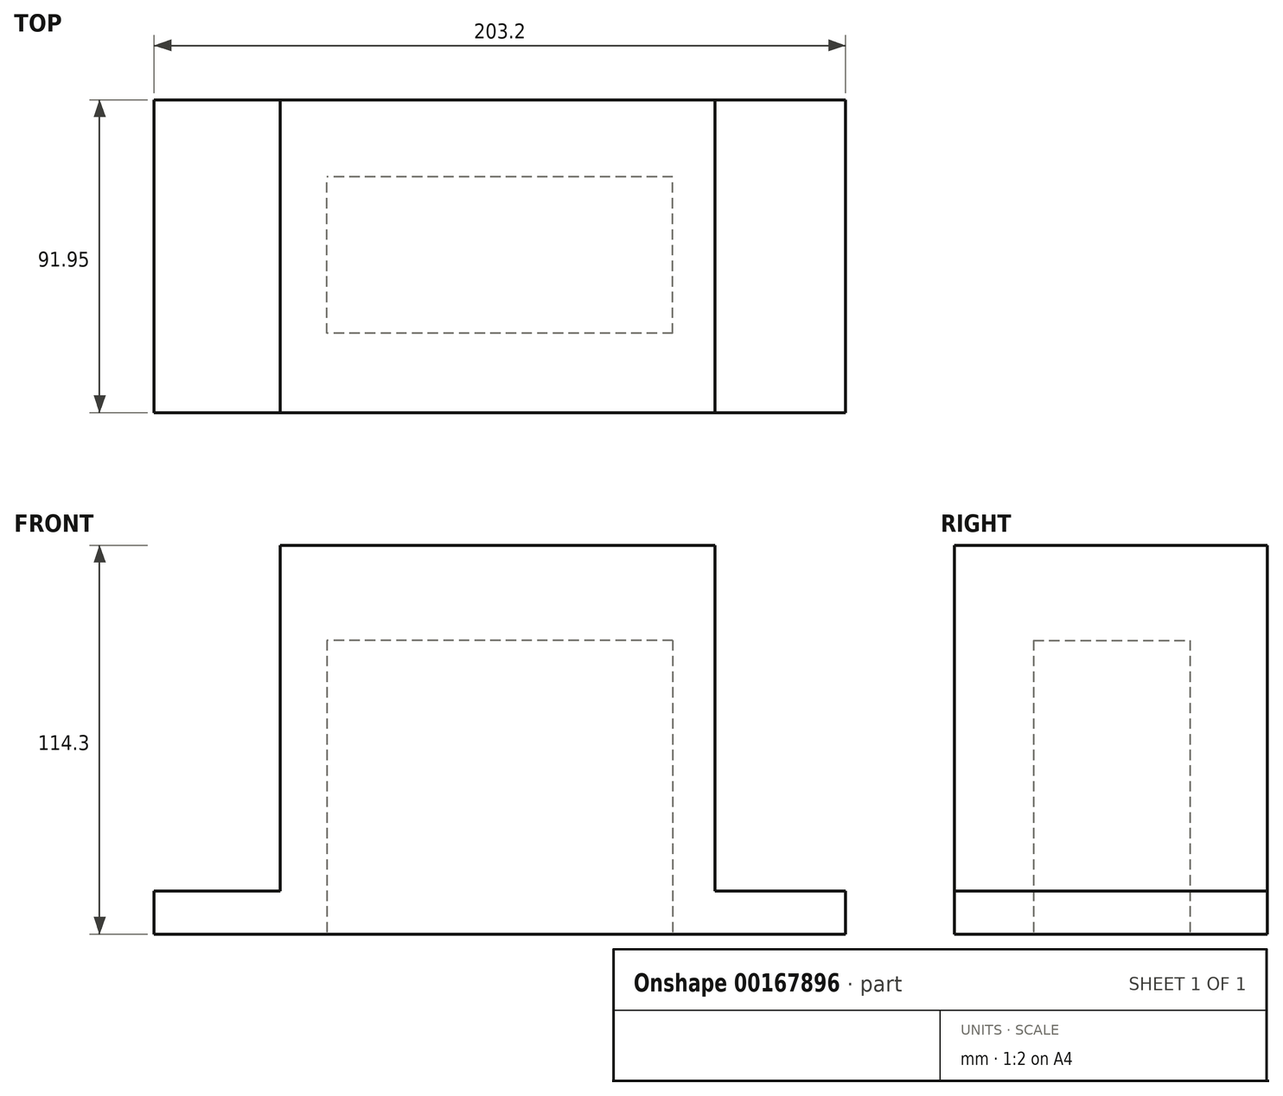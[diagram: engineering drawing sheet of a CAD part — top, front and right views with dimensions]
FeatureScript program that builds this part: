
annotation { "Feature Type Name" : "Feature", "Feature Type Description" : "" }
export const myFeature = defineFeature(function(context is Context, id is Id, definition is map)
    precondition{}
    {
        {
            var Q0;
            Q0=qCreatedBy(makeId("Front.planeOp"),FACE);
            var sketch = newSketch(context, id + "F0", { "sketchPlane" : qUnion([Q0])});
            skLineSegment(sketch, "E0.bottom", {"start": v(76.2, 57.15) * mm, "end": v(-76.2, 57.15) * mm});
            skLineSegment(sketch, "E0.top", {"start": v(76.2, -57.15) * mm, "end": v(-76.2, -57.15) * mm});
            skLineSegment(sketch, "E0.left", {"start": v(76.2, 57.15) * mm, "end": v(76.2, -57.15) * mm});
            skLineSegment(sketch, "E0.right", {"start": v(-76.2, 57.15) * mm, "end": v(-76.2, -57.15) * mm});
            skPoint(sketch, "E0.middle", {"position": v(0, 0) * mm});
            skSolve(sketch);
        }
        {
            var Q0;
            Q0=makeQuery(id+"F0.imprint","IMPRINT",FACE,{"disambiguationData":[TD([[makeQuery(id+"F0.imprint","IMPRINT",EDGE,{"derivedFrom":sQuery(id+"F0.wireOp",EDGE,"E0.bottom")}),1.0]])]});
            extrude(context, id + "F1", {"entities" : qUnion([Q0]), "oppositeDirection" : true, "depth" : 91.95 * mm});
        }
        {
            var Q0;
            Q0=makeQuery(id+"F1.opExtrude","SWEPT_FACE",FACE,{"disambiguationData":[OSD([sQuery(id+"F0.wireOp",EDGE,"E0.left")])]});
            var sketch = newSketch(context, id + "F2", { "sketchPlane" : qUnion([Q0])});
            skLineSegment(sketch, "E1", {"start": v(0, -57.15) * mm, "end": v(0, -44.45) * mm});
            skLineSegment(sketch, "E2", {"start": v(0, -44.45) * mm, "end": v(-62.9, -1.45) * mm});
            skLineSegment(sketch, "E3", {"start": v(-62.9, -1.45) * mm, "end": v(-62.9, 98.04) * mm});
            skLineSegment(sketch, "E4", {"start": v(-62.9, 98.04) * mm, "end": v(31.97, 98.04) * mm});
            skLineSegment(sketch, "E5", {"start": v(31.97, 98.04) * mm, "end": v(91.95, 57.15) * mm});
            skLineSegment(sketch, "E6", {"start": v(91.95, 57.15) * mm, "end": v(91.95, -44.45) * mm});
            skLineSegment(sketch, "E7", {"start": v(91.95, -44.45) * mm, "end": v(0, -44.45) * mm});
            skSolve(sketch);
        }
        {
            var Q0;
            Q0=makeQuery(id+"F2.imprint","IMPRINT",FACE,{"disambiguationData":[TD([[makeQuery(id+"F2.imprint","IMPRINT",EDGE,{"derivedFrom":sQuery(id+"F2.wireOp",EDGE,"E6")}),-1.0]])]});
            extrude(context, id + "F3", {"entities" : qUnion([Q0]), "operationType" : NewBodyOperationType.REMOVE, "oppositeDirection" : true, "depth" : 37.08 * mm});
        }
        {
            var Q0;
            Q0=makeQuery(id+"F1.opExtrude","SWEPT_FACE",FACE,{"disambiguationData":[OSD([sQuery(id+"F0.wireOp",EDGE,"E0.right")])]});
            var sketch = newSketch(context, id + "F4", { "sketchPlane" : qUnion([Q0])});
            skLineSegment(sketch, "E8", {"start": v(0, -57.15) * mm, "end": v(0, -44.45) * mm});
            skLineSegment(sketch, "E9", {"start": v(0, -44.45) * mm, "end": v(87.77, 57.15) * mm});
            skLineSegment(sketch, "E10", {"start": v(0, -44.45) * mm, "end": v(-91.95, -44.45) * mm});
            skSolve(sketch);
        }
        {
            var Q0;
            {var subQ0=sQuery(id+"F4.wireOp",EDGE,"E10");Q0=makeQuery(id+"F4.imprint","IMPRINT",FACE,{"disambiguationData":[TD([[makeQuery(id+"F4.imprint","IMPRINT",EDGE,{"derivedFrom":subQ0}),-1.0]])]});}
            extrude(context, id + "F5", {"entities" : qUnion([Q0]), "operationType" : NewBodyOperationType.REMOVE, "oppositeDirection" : true, "depth" : 37.08 * mm});
        }
        {
            var Q0;
            Q0=makeQuery(id+"F3.boolean.opBoolean","COPY",FACE,{"derivedFrom":makeQuery(id+"F3.opExtrude","CAP_FACE",FACE,{"disambiguationData":[OSD([sQuery(id+"F0.wireOp",EDGE,"E0.bottom"),sQuery(id+"F0.wireOp",EDGE,"E0.left"),sQuery(id+"F2.wireOp",EDGE,"E6"),sQuery(id+"F2.wireOp",EDGE,"E7")])],"isStart":false})});
            extrude(context, id + "F6", {"entities" : qUnion([Q0]), "operationType" : NewBodyOperationType.ADD, "depth" : 24.13 * mm});
        }
        {
            var Q0;
            Q0=makeQuery(id+"F5.boolean.opBoolean","COPY",FACE,{"derivedFrom":makeQuery(id+"F5.opExtrude","CAP_FACE",FACE,{"disambiguationData":[OSD([sQuery(id+"F0.wireOp",EDGE,"E0.bottom"),sQuery(id+"F0.wireOp",EDGE,"E0.right"),sQuery(id+"F4.wireOp",EDGE,"E10")])],"isStart":false})});
            extrude(context, id + "F7", {"entities" : qUnion([Q0]), "operationType" : NewBodyOperationType.ADD, "depth" : 25.4 * mm});
        }
        {
            var Q0;
            Q0=makeQuery(id+"F1.opExtrude","SWEPT_FACE",FACE,{"disambiguationData":[OSD([sQuery(id+"F0.wireOp",EDGE,"E0.left")])]});
            extrude(context, id + "F8", {"entities" : qUnion([Q0]), "operationType" : NewBodyOperationType.ADD, "depth" : 25.4 * mm});
        }
        {
            var Q0;
            Q0=makeQuery(id+"F1.opExtrude","SWEPT_FACE",FACE,{"disambiguationData":[OSD([sQuery(id+"F0.wireOp",EDGE,"E0.right")])]});
            extrude(context, id + "F9", {"entities" : qUnion([Q0]), "operationType" : NewBodyOperationType.ADD, "depth" : 25.4 * mm});
        }
        {
            var Q0;
            {var subQ0=sQuery(id+"F0.wireOp",EDGE,"E0.top");Q0=makeQuery(id+"F9.boolean.opBoolean","MERGE",FACE,{"derivedFrom":[makeQuery(id+"F8.boolean.opBoolean","MERGE",FACE,{"derivedFrom":[makeQuery(id+"F1.opExtrude","SWEPT_FACE",FACE,{"disambiguationData":[OSD([subQ0])]}),makeQuery(id+"F8.opExtrude","SWEPT_FACE",FACE,{"disambiguationData":[OSD([subQ0,sQuery(id+"F0.wireOp",EDGE,"E0.left")])]})]}),makeQuery(id+"F9.opExtrude","SWEPT_FACE",FACE,{"disambiguationData":[OSD([subQ0,sQuery(id+"F0.wireOp",EDGE,"E0.right")])]})]});}
            var sketch = newSketch(context, id + "F10", { "sketchPlane" : qUnion([Q0])});
            skLineSegment(sketch, "E11", {"start": v(0, -91.95) * mm, "end": v(0, -45.97) * mm});
            skPoint(sketch, "E11.endSnap0", {"position": v(0, 0) * mm});
            skSolve(sketch);
        }
        {
            var Q0;
            {var subQ1=sQuery(id+"F0.wireOp",EDGE,"E0.top");var subQ2=sQuery(id+"F0.wireOp",EDGE,"E0.left");var subQ4=makeQuery(id+"F8.opExtrude","CAP_EDGE",EDGE,{"disambiguationData":[OSD([subQ1,subQ2])],"isStart":false});Q0=makeQuery(id+"F10.imprint","IMPRINT",FACE,{"disambiguationData":[TD([[makeQuery(id+"F10.imprint","IMPRINT",EDGE,{"derivedFrom":subQ4}),1.0]])]});}
            var sketch = newSketch(context, id + "F11", { "sketchPlane" : qUnion([Q0])});
            skLineSegment(sketch, "E12.bottom", {"start": v(50.8, -23.25) * mm, "end": v(-50.8, -23.25) * mm});
            skLineSegment(sketch, "E12.top", {"start": v(50.8, -69.22) * mm, "end": v(-50.8, -69.22) * mm});
            skLineSegment(sketch, "E12.left", {"start": v(50.8, -23.25) * mm, "end": v(50.8, -69.22) * mm});
            skLineSegment(sketch, "E12.right", {"start": v(-50.8, -23.25) * mm, "end": v(-50.8, -69.22) * mm});
            skPoint(sketch, "E12.middle", {"position": v(0, -46.23) * mm});
            skSolve(sketch);
        }
        {
            var Q0;
            Q0=makeQuery(id+"F11.imprint","IMPRINT",FACE,{"disambiguationData":[TD([[makeQuery(id+"F11.imprint","IMPRINT",EDGE,{"derivedFrom":sQuery(id+"F11.wireOp",EDGE,"E12.bottom")}),1.0]])]});
            extrude(context, id + "F12", {"entities" : qUnion([Q0]), "operationType" : NewBodyOperationType.REMOVE, "oppositeDirection" : true, "depth" : 86.36 * mm});
        }
    });
